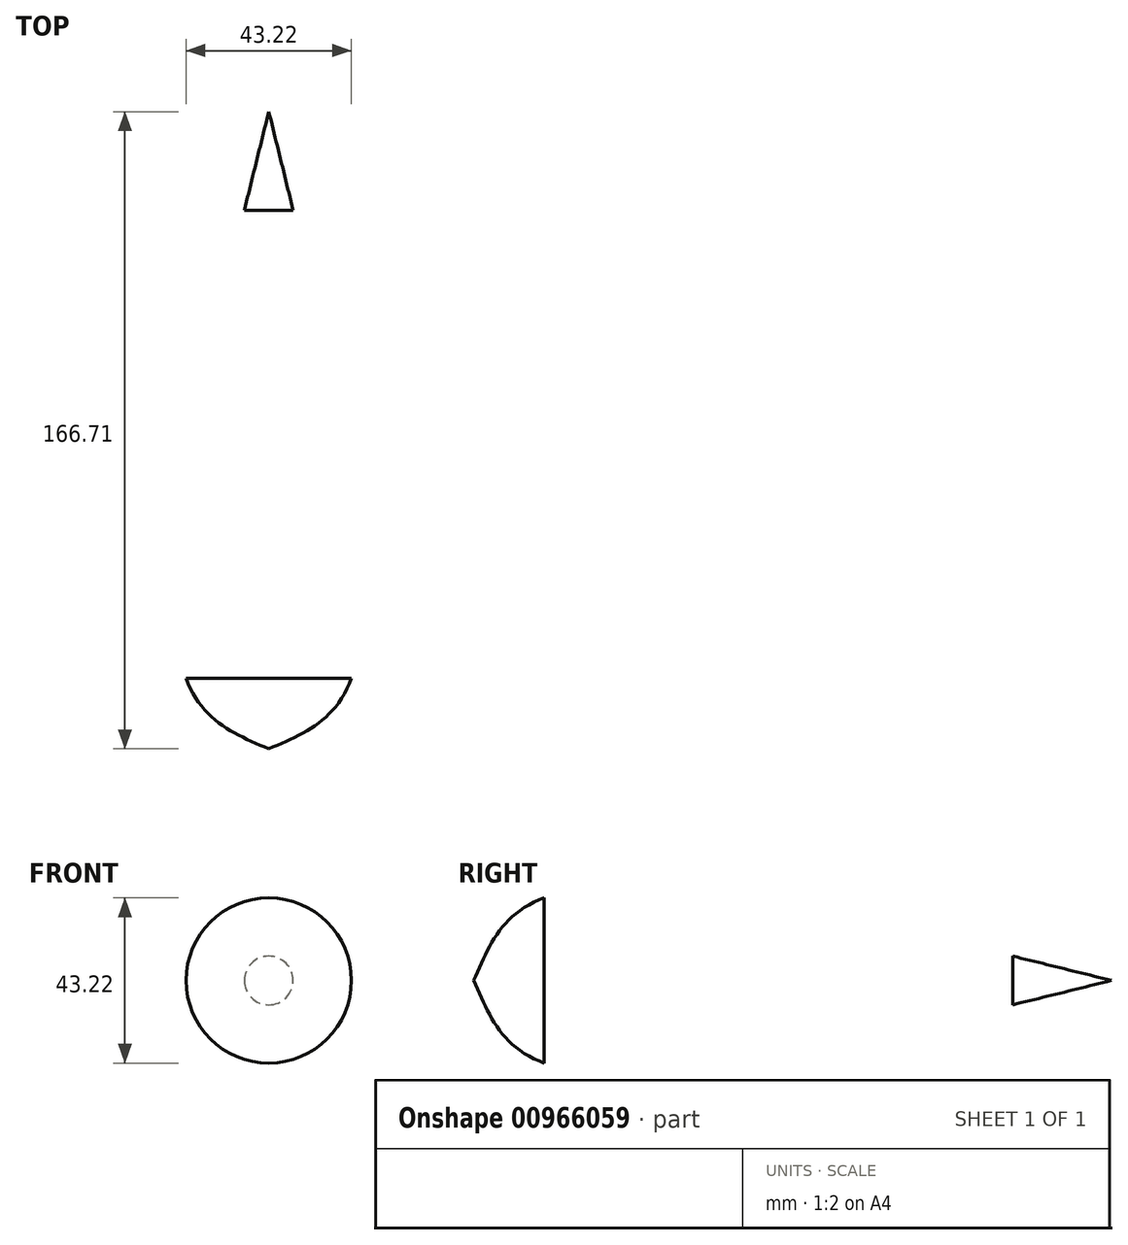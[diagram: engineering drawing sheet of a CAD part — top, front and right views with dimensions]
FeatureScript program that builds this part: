
annotation { "Feature Type Name" : "Feature", "Feature Type Description" : "" }
export const myFeature = defineFeature(function(context is Context, id is Id, definition is map)
    precondition{}
    {
        {
            var Q0;
            Q0=qCreatedBy(makeId("Top.planeOp"),FACE);
            var sketch = newSketch(context, id + "F0", { "sketchPlane" : qUnion([Q0])});
            skFitSpline(sketch, "E0", {"points": [v(0, -64.47) * mm, v(-21.4, -46.62) * mm, v(0, 102.24) * mm], "startDerivative": vector(-86.43, 36.2) * mm, "endDerivative": vector(66.18, 266.63) * mm});
            skLineSegment(sketch, "E1", {"start": v(-6.37, 76.42) * mm, "end": v(0, 76.42) * mm});
            skLineSegment(sketch, "E2", {"start": v(0, 76.42) * mm, "end": v(0, 102.24) * mm});
            skLineSegment(sketch, "E3", {"start": v(0, 76.42) * mm, "end": v(0, -46.07) * mm});
            skLineSegment(sketch, "E4", {"start": v(0, -46.07) * mm, "end": v(-21.6, -46.07) * mm});
            skArc(sketch, "E5", {"start": v(-118.14, -15.13) * mm, "mid": v(-32.19, 0) * mm, "end": v(-118.14, 15.13) * mm});
            skArc(sketch, "E6", {"start": v(-57.67, 40.1) * mm, "mid": v(-36.18, 35.93) * mm, "end": v(-14.74, 40.4) * mm});
            skArc(sketch, "E7", {"start": v(-18.14, -78.35) * mm, "mid": v(-39.86, -56.98) * mm, "end": v(-67.1, -43.3) * mm});
            skCircle(sketch, "E8", {"center": v(0, -121.69) * mm, "radius": 46.98 * mm});
            skArc(sketch, "E9", {"start": v(-153.5, 12.57) * mm, "mid": v(-235.53, 0) * mm, "end": v(-153.5, -12.57) * mm});
            skArc(sketch, "E10", {"start": v(-118.14, -15.13) * mm, "mid": v(-135.63, -11.26) * mm, "end": v(-153.5, -12.57) * mm});
            skPoint(sketch, "E11.orphan", {"position": v(-85.9, -43.3) * mm});
            skPoint(sketch, "E12.orphan", {"position": v(-193.55, -41.98) * mm});
            skArc(sketch, "E13.MirrorCS", {"start": v(-118.14, 15.13) * mm, "mid": v(-135.63, 11.26) * mm, "end": v(-153.5, 12.57) * mm});
            skLineSegment(sketch, "E14", {"start": v(0, -64.47) * mm, "end": v(0, -46.07) * mm});
            skLineSegment(sketch, "E15", {"start": v(0, -64.47) * mm, "end": v(0, -74.7) * mm});
            skSolve(sketch);
        }
        {
            var Q0;
            {var subQ2=sQuery(id+"F0.wireOp",EDGE,"E4");Q0=makeQuery(id+"F0.imprint","IMPRINT",FACE,{"disambiguationData":[TD([[makeQuery(id+"F0.imprint","IMPRINT",EDGE,{"derivedFrom":subQ2}),1.0]])]});}
            var Q1;
            Q1=sQuery(id+"F0.wireOp",EDGE,"E14");
            revolve(context, id + "F1", {"surfaceOperationType" : NewSurfaceOperationType.NEW, "entities" : qUnion([Q0]), "axis" : qUnion([Q1]), "revolveType" : RevolveType.FULL});
        }
        {
            var Q0;
            {var subQ2=sQuery(id+"F0.wireOp",EDGE,"E1");Q0=makeQuery(id+"F0.imprint","IMPRINT",FACE,{"disambiguationData":[TD([[makeQuery(id+"F0.imprint","IMPRINT",EDGE,{"derivedFrom":subQ2}),1.0]])]});}
            var Q1;
            Q1=sQuery(id+"F0.wireOp",EDGE,"E2");
            revolve(context, id + "F2", {"surfaceOperationType" : NewSurfaceOperationType.NEW, "entities" : qUnion([Q0]), "axis" : qUnion([Q1]), "revolveType" : RevolveType.FULL});
        }
    });
